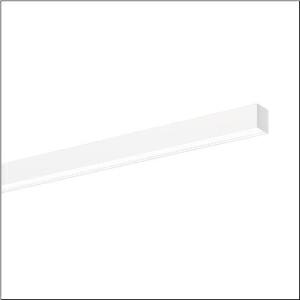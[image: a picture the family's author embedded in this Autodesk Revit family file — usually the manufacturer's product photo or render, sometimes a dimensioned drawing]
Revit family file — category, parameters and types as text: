
# Revit family: silica_r__21_51mx20db42wb_d1f2
name_source: partatom
category: Lighting Fixtures
units: mm (PartAtom-declared; Revit-internal decimal feet)

## family parameters
Cut with Voids When Loaded = No
Host = Face
Light Source = No
Part Type = Normal
Room Calculation Point = No
Round Connector Dimension = Use Diameter
Shared = No

## types (1)
- --- (1 x LED, 3000 lm, 19 W, 4000K)
    Apparent Load = 19 VA
    CIE Flux Codes = 48 79 96 100 100
    Color Rendering = 80
    Color Temperature = 4000K
    Default Elevation = 1800 mm
    Description = Silica® 21, office luminaire, primary optical cover: cover, of PMMA, opal, light emission: direct distribution, primary light characteristic: symmetric, installation type: surface-mounted, LED, rated luminous flux: 3.000lm, luminous efficacy: 158lm/W, light colour: 840, colour temperature: 4000K, with terminal, 3+2-pole, max. 2.5mm², mains connection: 220..240V, AC, 50/60Hz, rated input power: 19W, luminaire housing, of aluminium, traffic white (RAL 9016), length: 1.504mm, width: 53mm, height: 53mm, protection rating (complete): IP20, insulation class (complete): insulation class I (protective earthing), certification: CE, permissible operating ambient temperature: 0..+35°C, standard: EN 50419, packaging unit: 1 piece
    Height = 0 mm  [stored 0 ft]
    Lamp = 1 x LED
    Lamp Light Flux = 3000 lm
    Lamp Power = 19 W
    Lamp count = 1
    Length = 1504 mm
    Luminous efficacy = 158 lm/W
    Manufacturer = Siteco
    ModVariant = No
    Model = 51MX20DB42WB
    Mounting Place = Ceiling
    Mounting Type = Recessed
    Number of Poles = 1
    OnlyDefault = Yes
    Power Factor = 1
    Product Name = Silica® 21
    Product group = office luminaire | ceiling recessed
    ProductGroupID = 401
    Protection Class = Protection class I
    Protection Degree = IP 20
    RLX_Detail_Level = 1
    RLX_Emergency_Light_Flux = 0 lm
    RLX_Emergency_Type = 0
    RLX_Emergency_Type_DB = No
    RlxData = <blob elided: 23781 chars, md5=68ccbcac>
    Socket = socket
    Standby Power = 0 W
    System Light Flux = 3000 lm
    System Power = 19 W
    Type Comments = factory setting: luminous flux: 100 % | dim-lin: 254 | 218 mA
    Type Image = l_1297777.jpg
    URL = http://relux.com
    VarID = @adj_048449
    Voltage = 0 V
    Weight = 0.00 kg
    Width = 53 mm

note: [stored X ft] marks values corroborated as IEEE doubles in the binary element streams (Revit-internal decimal feet)

## geometry (parser evidence)
native form markers: Blend x4, Sweep x9
no freeform markers — native parametric forms only
